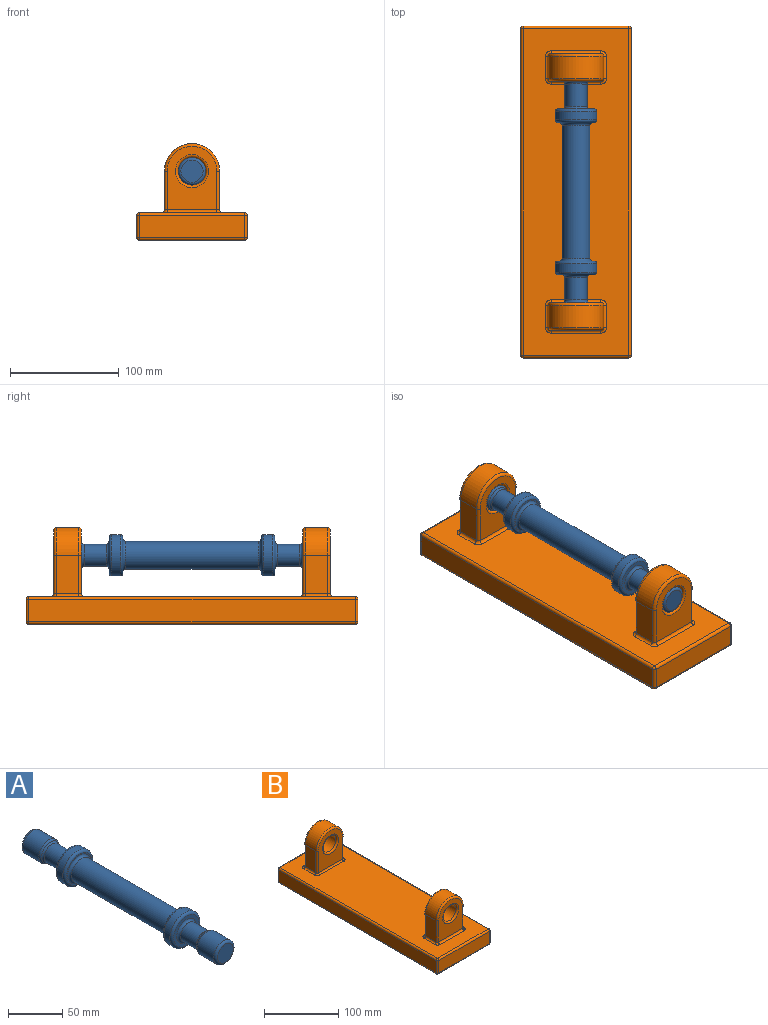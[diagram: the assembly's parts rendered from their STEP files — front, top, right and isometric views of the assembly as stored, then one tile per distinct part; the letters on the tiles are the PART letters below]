
ASSEMBLY  parts=2 mates=1
PART A: 27 faces, bbox 41.2x254x41.2 mm
  f0: cylinder r=19.05mm len=38.1mm, axis (0,1,0), area 912.1mm2, adj f20,f21
  f1: plane 33.02x33.02mm, normal (0,1,0), area 349.6mm2, adj f15,f21
  f2: plane 20.32x20.32mm, normal (0,1,0), area 324.3mm2, adj f25
  f3: cylinder r=12.7mm len=25.4mm, axis (0,1,0), area 1675.8mm2, adj f24,f25
  f4: cylinder r=10.16mm len=20.32mm, axis (0,-1,0), area 1297.2mm2, adj f15,f18
  f5: cylinder r=12.7mm len=121.92mm, axis (0,-1,0), area 9728.8mm2, adj f13,f14
  f6: plane 33.02x33.02mm, normal (0,-1,0), area 126.7mm2, adj f14,f20
  f7: plane 33.02x33.02mm, normal (0,1,0), area 126.7mm2, adj f13,f19
  f8: plane 20.32x20.32mm, normal (0,-1,0), area 324.3mm2, adj f26
  f9: cylinder r=12.7mm len=25.4mm, axis (0,1,0), area 1675.8mm2, adj f23,f26
  f10: cylinder r=10.16mm len=20.32mm, axis (0,-1,0), area 1297.2mm2, adj f16,f17
  f11: plane 33.02x33.02mm, normal (0,-1,0), area 349.6mm2, adj f16,f22
  f12: cylinder r=19.05mm len=38.1mm, axis (0,1,0), area 912.1mm2, adj f19,f22
  f13: torus R=15.24mm, axis (0,-1,0), area 341.5mm2, adj f5,f7
  f14: torus R=15.24mm, axis (0,-1,0), area 341.5mm2, adj f5,f6
  f15: torus R=12.7mm, axis (0,-1,0), area 277.8mm2, adj f1,f4
  f16: torus R=12.7mm, axis (0,-1,0), area 277.8mm2, adj f10,f11
  f17: torus R=12.7mm, axis (0,-1,0), area 177.1mm2, adj f10,f23
  f18: torus R=12.7mm, axis (0,-1,0), area 177.1mm2, adj f4,f24
  f19: torus R=16.51mm, axis (0,-1,0), area 454.4mm2, adj f7,f12
  f20: torus R=16.51mm, axis (0,-1,0), area 454.4mm2, adj f0,f6
  f21: torus R=16.51mm, axis (0,-1,0), area 454.4mm2, adj f0,f1
  f22: torus R=16.51mm, axis (0,-1,0), area 454.4mm2, adj f11,f12
  f23: torus R=10.16mm, axis (0,1,0), area 204.9mm2, adj f9,f17
  f24: torus R=10.16mm, axis (0,1,0), area 204.9mm2, adj f3,f18
  f25: torus R=10.16mm, axis (0,-1,0), area 295.2mm2, adj f2,f3
  f26: torus R=10.16mm, axis (0,-1,0), area 295.2mm2, adj f8,f9
PART B: 70 faces, bbox 101.6x304.8x91 mm
  f0: cylinder r=25.4mm len=50.8mm, axis (0,-1,0), area 1621.5mm2, adj f1,f3,f7,f11
  f1: plane 35.56x20.32mm, normal (-1,0,0), area 722.6mm2, adj f0,f8,f12,f42
  f2: cylinder r=12.7mm len=25.4mm, axis (0,-1,0), area 1621.5mm2, adj f6,f10
  f3: plane 35.56x20.32mm, normal (1,0,0), area 722.6mm2, adj f0,f9,f13,f45
  f4: plane 58.42x45.72mm, normal (0,1,0), area 1717mm2, adj f10,f11,f12,f13,f41
  f5: plane 58.42x45.72mm, normal (0,-1,0), area 1717mm2, adj f6,f7,f8,f9,f46
  f6: torus R=15.24mm, axis (0,-1,0), area 341.5mm2, adj f2,f5
  f7: torus R=22.86mm, axis (0,-1,0), area 306.8mm2, adj f0,f5,f8,f9
  f8: cylinder r=2.54mm len=35.56mm, axis (0,0,-1), area 141.9mm2, adj f1,f5,f7,f44
  f9: cylinder r=2.54mm len=35.56mm, axis (0,0,1), area 141.9mm2, adj f3,f5,f7,f47
  f10: torus R=15.24mm, axis (0,-1,0), area 341.5mm2, adj f2,f4
  f11: torus R=22.86mm, axis (0,-1,0), area 306.8mm2, adj f0,f4,f12,f13
  f12: cylinder r=2.54mm len=35.56mm, axis (0,0,1), area 141.9mm2, adj f1,f4,f11,f40
  f13: cylinder r=2.54mm len=35.56mm, axis (0,0,-1), area 141.9mm2, adj f3,f4,f11,f43
  f14: plane 299.72x96.52mm, normal (0,0,1), area 25566.8mm2, adj f28,f33,f36,f39,f40,f41,f42,f43
  f15: plane 299.72x20.32mm, normal (-1,0,0), area 6090.3mm2, adj f25,f34,f35,f39
  f16: plane 299.72x96.52mm, normal (0,0,-1), area 28929mm2, adj f20,f24,f25,f26
  f17: plane 299.72x20.32mm, normal (1,0,0), area 6090.3mm2, adj f20,f23,f27,f28
  f18: plane 96.52x20.32mm, normal (0,-1,0), area 1961.3mm2, adj f23,f24,f33,f34
  f19: plane 96.52x20.32mm, normal (0,1,0), area 1961.3mm2, adj f26,f27,f35,f36
  f20: cylinder r=2.54mm len=299.72mm, axis (0,-1,0), area 1195.8mm2, adj f16,f17,f21,f22
  f21: sphere r=2.54mm, area 10.1mm2, adj f20,f23,f24
  f22: sphere r=2.54mm, area 10.1mm2, adj f20,f26,f27
  f23: cylinder r=2.54mm len=20.32mm, axis (0,0,-1), area 81.1mm2, adj f17,f18,f21,f29
  f24: cylinder r=2.54mm len=96.52mm, axis (-1,0,0), area 385.1mm2, adj f16,f18,f21,f30
  f25: cylinder r=2.54mm len=299.72mm, axis (0,1,0), area 1195.8mm2, adj f15,f16,f30,f31
  f26: cylinder r=2.54mm len=96.52mm, axis (1,0,0), area 385.1mm2, adj f16,f19,f22,f31
  f27: cylinder r=2.54mm len=20.32mm, axis (0,0,1), area 81.1mm2, adj f17,f19,f22,f32
  f28: cylinder r=2.54mm len=299.72mm, axis (0,1,0), area 1195.8mm2, adj f14,f17,f29,f32
  f29: sphere r=2.54mm, area 10.1mm2, adj f23,f28,f33
  f30: sphere r=2.54mm, area 10.1mm2, adj f24,f25,f34
  f31: sphere r=2.54mm, area 10.1mm2, adj f25,f26,f35
  f32: sphere r=2.54mm, area 10.1mm2, adj f27,f28,f36
  f33: cylinder r=2.54mm len=96.52mm, axis (1,0,0), area 385.1mm2, adj f14,f18,f29,f37
  f34: cylinder r=2.54mm len=20.32mm, axis (0,0,1), area 81.1mm2, adj f15,f18,f30,f37
  f35: cylinder r=2.54mm len=20.32mm, axis (0,0,-1), area 81.1mm2, adj f15,f19,f31,f38
  f36: cylinder r=2.54mm len=96.52mm, axis (-1,0,0), area 385.1mm2, adj f14,f19,f32,f38
  f37: sphere r=2.54mm, area 10.1mm2, adj f33,f34,f39
  f38: sphere r=2.54mm, area 10.1mm2, adj f35,f36,f39
  f39: cylinder r=2.54mm len=299.72mm, axis (0,-1,0), area 1195.8mm2, adj f14,f15,f37,f38
  f40: torus R=5.08mm, axis (0,0,1), area 21.7mm2, adj f12,f14,f41,f42
  f41: cylinder r=2.54mm len=45.72mm, axis (-1,0,0), area 182.4mm2, adj f4,f14,f40,f43
  f42: cylinder r=2.54mm len=20.32mm, axis (0,1,0), area 81.1mm2, adj f1,f14,f40,f44
  f43: torus R=5.08mm, axis (0,0,1), area 21.7mm2, adj f13,f14,f41,f45
  f44: torus R=5.08mm, axis (0,0,1), area 21.7mm2, adj f8,f14,f42,f46
  f45: cylinder r=2.54mm len=20.32mm, axis (0,-1,0), area 81.1mm2, adj f3,f14,f43,f47
  f46: cylinder r=2.54mm len=45.72mm, axis (1,0,0), area 182.4mm2, adj f5,f14,f44,f47
  f47: torus R=5.08mm, axis (0,0,1), area 21.7mm2, adj f9,f14,f45,f46
  f48: cylinder r=25.4mm len=50.8mm, axis (0,1,0), area 1621.5mm2, adj f49,f51,f55,f59
  f49: plane 35.56x20.32mm, normal (-1,0,0), area 722.6mm2, adj f48,f56,f60,f64
  f50: cylinder r=12.7mm len=25.4mm, axis (0,1,0), area 1621.5mm2, adj f54,f58
  f51: plane 35.56x20.32mm, normal (1,0,0), area 722.6mm2, adj f48,f57,f61,f67
  f52: plane 58.42x45.72mm, normal (0,-1,0), area 1717mm2, adj f58,f59,f60,f61,f63
  f53: plane 58.42x45.72mm, normal (0,1,0), area 1717mm2, adj f54,f55,f56,f57,f68
  f54: torus R=15.24mm, axis (0,1,0), area 341.5mm2, adj f50,f53
  f55: torus R=22.86mm, axis (0,1,0), area 306.8mm2, adj f48,f53,f56,f57
  f56: cylinder r=2.54mm len=35.56mm, axis (0,0,-1), area 141.9mm2, adj f49,f53,f55,f66
  f57: cylinder r=2.54mm len=35.56mm, axis (0,0,1), area 141.9mm2, adj f51,f53,f55,f69
  f58: torus R=15.24mm, axis (0,1,0), area 341.5mm2, adj f50,f52
  f59: torus R=22.86mm, axis (0,1,0), area 306.8mm2, adj f48,f52,f60,f61
  f60: cylinder r=2.54mm len=35.56mm, axis (0,0,1), area 141.9mm2, adj f49,f52,f59,f62
  f61: cylinder r=2.54mm len=35.56mm, axis (0,0,-1), area 141.9mm2, adj f51,f52,f59,f65
  f62: torus R=5.08mm, axis (0,0,1), area 21.7mm2, adj f14,f60,f63,f64
  f63: cylinder r=2.54mm len=45.72mm, axis (-1,0,0), area 182.4mm2, adj f14,f52,f62,f65
  f64: cylinder r=2.54mm len=20.32mm, axis (0,-1,0), area 81.1mm2, adj f14,f49,f62,f66
  f65: torus R=5.08mm, axis (0,0,1), area 21.7mm2, adj f14,f61,f63,f67
  f66: torus R=5.08mm, axis (0,0,1), area 21.7mm2, adj f14,f56,f64,f68
  f67: cylinder r=2.54mm len=20.32mm, axis (0,1,0), area 81.1mm2, adj f14,f51,f65,f69
  f68: cylinder r=2.54mm len=45.72mm, axis (1,0,0), area 182.4mm2, adj f14,f53,f66,f69
  f69: torus R=5.08mm, axis (0,0,1), area 21.7mm2, adj f14,f57,f67,f68
PLACE A rot(axis=(0,1,0),180deg) t=(-2.47,-2.07,18.08)mm
PLACE B t=(-2.47,-2.07,18.08)mm fixed
MATE revolute A.f3 <-> B.f0  axis (0,-1,0) through (-2.47,-129.07,18.08)mm
